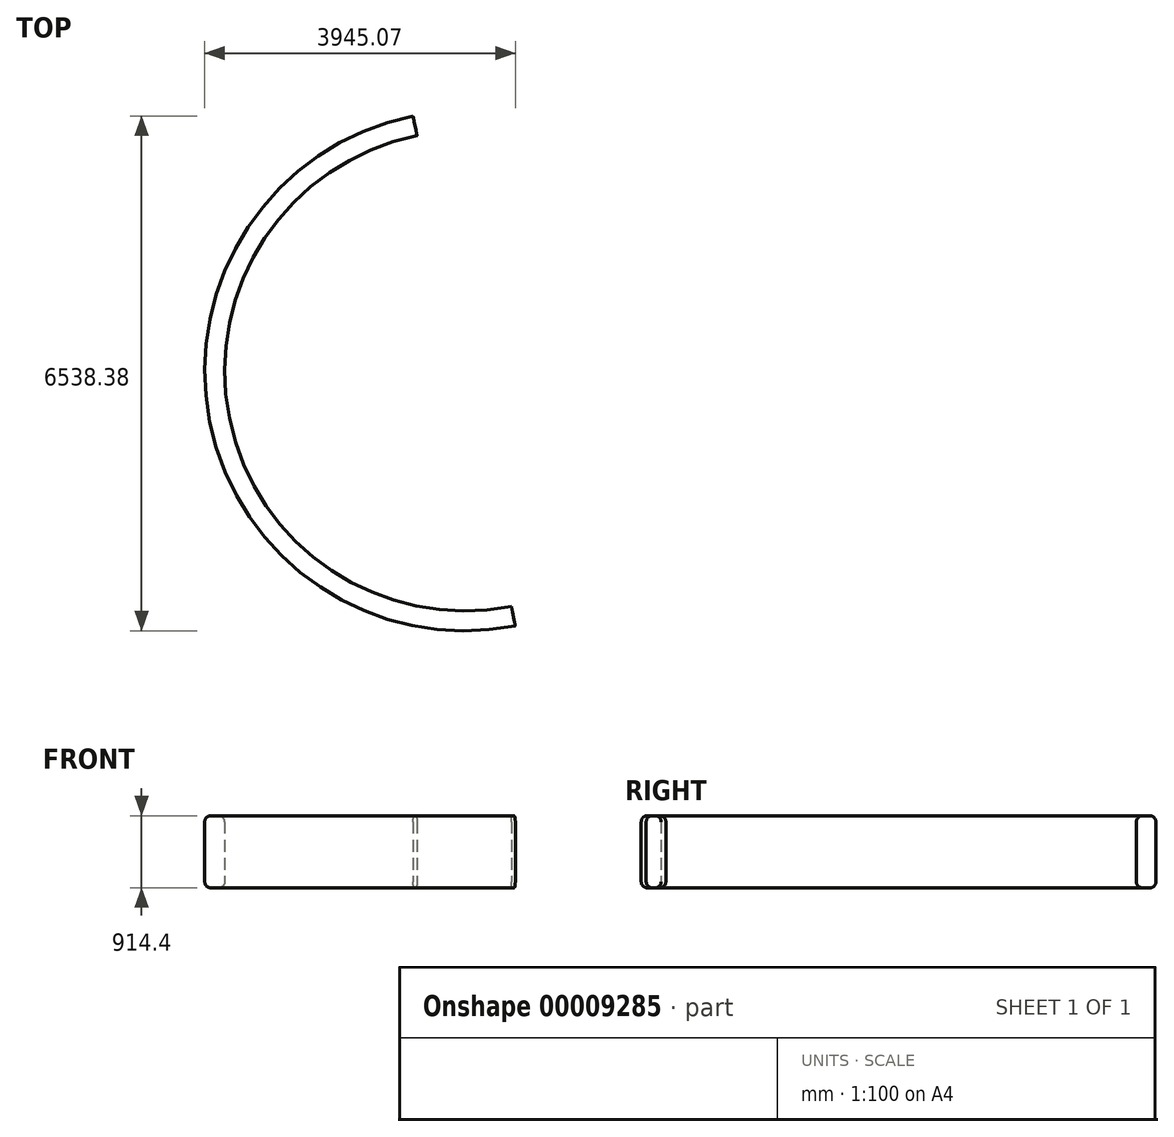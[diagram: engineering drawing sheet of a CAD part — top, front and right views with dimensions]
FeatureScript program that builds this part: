
annotation { "Feature Type Name" : "Feature", "Feature Type Description" : "" }
export const myFeature = defineFeature(function(context is Context, id is Id, definition is map)
    precondition{}
    {
        {
            var Q0;
            Q0=qCreatedBy(makeId("Top.planeOp"),FACE);
            var sketch = newSketch(context, id + "F0", { "sketchPlane" : qUnion([Q0])});
            skArc(sketch, "E0", {"start": v(-605.07, 2987.34) * mm, "mid": v(-2988.54, -599.1) * mm, "end": v(593.15, -2989.73) * mm});
            skArc(sketch, "E1", {"start": v(-655, 3236.38) * mm, "mid": v(-3237.58, -649.04) * mm, "end": v(643.07, -3238.77) * mm});
            skLineSegment(sketch, "E2", {"start": v(643.07, -3238.77) * mm, "end": v(593.15, -2989.73) * mm});
            skLineSegment(sketch, "E3.trimOffspring", {"start": v(-605.07, 2987.34) * mm, "end": v(-655, 3236.38) * mm});
            skSolve(sketch);
        }
        {
            var Q0;
            Q0=makeQuery(id+"F0.imprint","IMPRINT",FACE,{"disambiguationData":[TD([[makeQuery(id+"F0.imprint","IMPRINT",EDGE,{"derivedFrom":sQuery(id+"F0.wireOp",EDGE,"E0")}),-1.0]])]});
            extrude(context, id + "F1", {"entities" : qUnion([Q0]), "endBound" : BoundingType.SYMMETRIC, "depth" : 914.4 * mm, "hasSecondDirection" : true, "secondDirectionOppositeDirection" : true, "secondDirectionDepth" : 457.2 * mm});
        }
        {
            var Q0;
            Q0=makeQuery(id+"F1.opExtrude","CAP_EDGE",EDGE,{"disambiguationData":[OSD([sQuery(id+"F0.wireOp",EDGE,"E1")])],"isStart":false});
            var Q1;
            Q1=makeQuery(id+"F1.opExtrude","CAP_EDGE",EDGE,{"disambiguationData":[OSD([sQuery(id+"F0.wireOp",EDGE,"E0")])],"isStart":true});
            var Q2;
            Q2=makeQuery(id+"F1.opExtrude","CAP_EDGE",EDGE,{"disambiguationData":[OSD([sQuery(id+"F0.wireOp",EDGE,"E1")])],"isStart":true});
            var Q3;
            Q3=makeQuery(id+"F1.opExtrude","CAP_EDGE",EDGE,{"disambiguationData":[OSD([sQuery(id+"F0.wireOp",EDGE,"E0")])],"isStart":false});
            fillet(context, id + "F2", {"entities" : qUnion([Q0, Q1, Q2, Q3]), "radius" : 76.2 * mm, "tangentPropagation" : true, "allowEdgeOverflow" : false});
        }
    });
